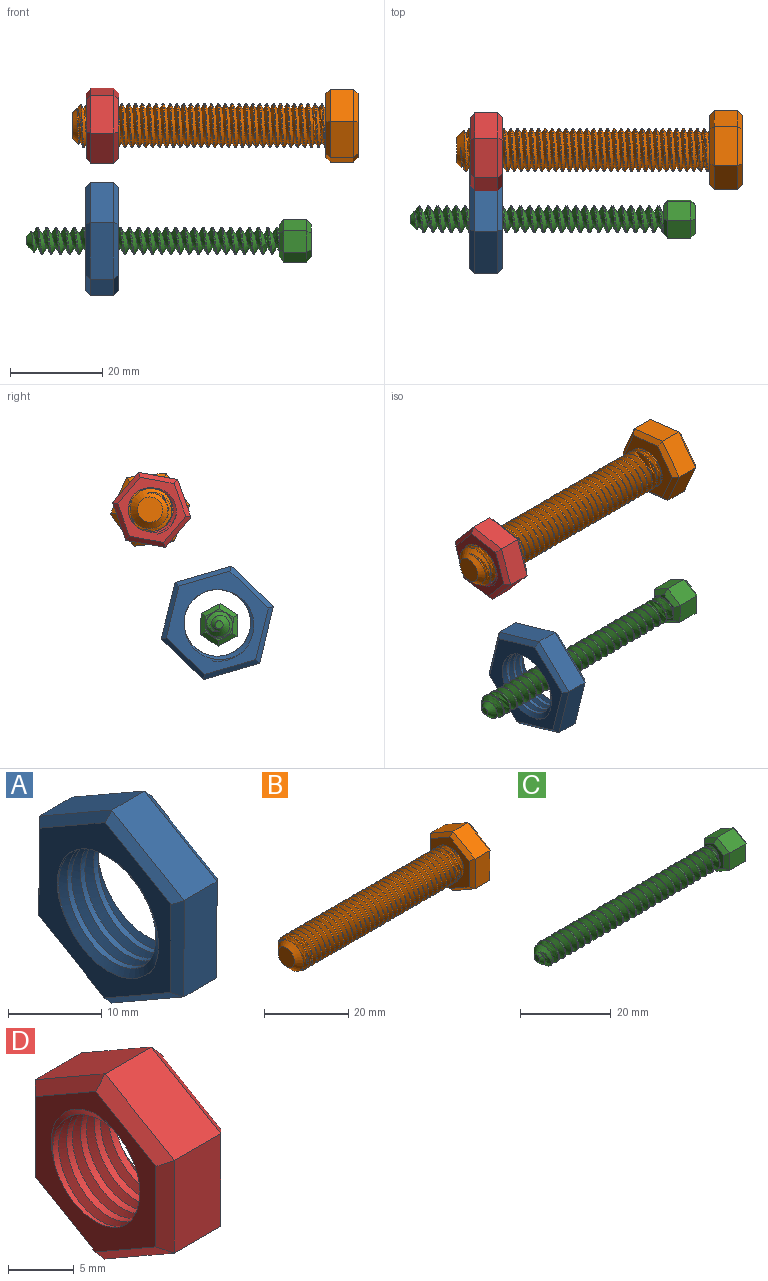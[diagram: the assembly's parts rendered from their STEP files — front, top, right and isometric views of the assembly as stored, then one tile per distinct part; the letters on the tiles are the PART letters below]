
ASSEMBLY  parts=4 mates=2
PART A: 23 faces, bbox 9.3x22.7x26 mm
  f0: cylinder r=7.24mm len=14.48mm, axis (1,0,0), area 111.6mm2, adj f7,f8,f21,f22
  f1: plane 10.98x6.38mm, normal (0,-0.5,0.86), area 63.5mm2, adj f2,f6,f14,f18
  f2: plane 12.7x5mm, normal (0,-1,0), area 63.5mm2, adj f1,f3,f12,f16
  f3: plane 11.02x6.32mm, normal (0,-0.5,-0.87), area 63.5mm2, adj f2,f4,f10,f15
  f4: plane 10.98x6.38mm, normal (0,0.5,-0.86), area 63.5mm2, adj f3,f5,f9,f17
  f5: plane 12.7x5mm, normal (0,1,0), area 63.5mm2, adj f4,f6,f11,f19
  f6: plane 11.02x6.32mm, normal (0,0.5,0.87), area 63.5mm2, adj f1,f5,f13,f20
  f7: plane 23.73x20.67mm, normal (-1,0,0), area 164.4mm2, adj f0,f9,f10,f11,f12,f13,f14,f21
  f8: plane 23.73x20.67mm, normal (1,0,0), area 164.4mm2, adj f0,f15,f16,f17,f18,f19,f20,f21
  f9: plane 10.99x6.96mm, normal (-0.71,0.36,-0.61), area 17.1mm2, adj f4,f7,f10,f11
  f10: plane 11.02x6.9mm, normal (-0.71,-0.35,-0.61), area 17.1mm2, adj f3,f7,f9,f12
  f11: plane 12.7x1.03mm, normal (-0.71,0.71,0), area 17.1mm2, adj f5,f7,f9,f13
  f12: plane 12.7x1.03mm, normal (-0.71,-0.71,0), area 17.1mm2, adj f2,f7,f10,f14
  f13: plane 11.02x6.9mm, normal (-0.71,0.35,0.61), area 17.1mm2, adj f6,f7,f11,f14
  f14: plane 10.99x6.96mm, normal (-0.71,-0.36,0.61), area 17.1mm2, adj f1,f7,f12,f13
  f15: plane 11.02x6.9mm, normal (0.71,-0.35,-0.61), area 17.1mm2, adj f3,f8,f16,f17
  f16: plane 12.7x1.03mm, normal (0.71,-0.71,0), area 17.1mm2, adj f2,f8,f15,f18
  f17: plane 10.99x6.96mm, normal (0.71,0.36,-0.61), area 17.1mm2, adj f4,f8,f15,f19
  f18: plane 10.99x6.96mm, normal (0.71,-0.36,0.61), area 17.1mm2, adj f1,f8,f16,f20
  f19: plane 12.7x1.03mm, normal (0.71,0.71,0), area 17.1mm2, adj f5,f8,f17,f20
  f20: plane 11.02x6.9mm, normal (0.71,0.35,0.61), area 17.1mm2, adj f6,f8,f18,f19
  f21: bspline ~19.31x16.73mm, area 223mm2, adj f0,f7,f8,f22
  f22: bspline ~19.31x16.73mm, area 223mm2, adj f0,f7,f8,f21
PART B: 25 faces, bbox 62.8x15.9x18.1 mm
  f0: cylinder r=4.75mm len=53mm, axis (1,0,0), area 256.1mm2, adj f1,f2,f4,f12
  f1: bspline ~55.16x10.97mm, area 1234.9mm2, adj f0,f2,f4,f12
  f2: bspline ~55.66x10.97mm, area 1234.1mm2, adj f0,f1,f4,f12
  f3: plane 5.5x5.5mm, normal (-1,0,0), area 23.8mm2, adj f4
  f4: cone r=4.75mm half-angle=45deg, axis (1,0,0), area 47.4mm2, adj f0,f1,f2,f3
  f5: plane 7.48x5mm, normal (0,-0.5,0.86), area 43.3mm2, adj f6,f10,f18,f22
  f6: plane 8.66x5mm, normal (0,-1,0), area 43.3mm2, adj f5,f7,f16,f20
  f7: plane 7.52x5mm, normal (0,-0.5,-0.87), area 43.3mm2, adj f6,f8,f14,f19
  f8: plane 7.48x5mm, normal (0,0.5,-0.86), area 43.3mm2, adj f7,f9,f13,f21
  f9: plane 8.66x5mm, normal (0,1,0), area 43.3mm2, adj f8,f10,f15,f23
  f10: plane 7.52x5mm, normal (0,0.5,0.87), area 43.3mm2, adj f5,f9,f17,f24
  f11: plane 15.01x13.03mm, normal (1,0,0), area 146.4mm2, adj f13,f14,f15,f16,f17,f18
  f12: plane 15.83x13.85mm, normal (-1,0,0), area 89.2mm2, adj f0,f1,f2,f19,f20,f21,f22,f23
  f13: plane 7.49x4.93mm, normal (0.71,0.36,-0.61), area 11.4mm2, adj f8,f11,f14,f15
  f14: plane 7.52x4.88mm, normal (0.71,-0.35,-0.61), area 11.4mm2, adj f7,f11,f13,f16
  f15: plane 8.66x1.03mm, normal (0.71,0.71,0), area 11.4mm2, adj f9,f11,f13,f17
  f16: plane 8.66x1.03mm, normal (0.71,-0.71,0), area 11.4mm2, adj f6,f11,f14,f18
  f17: plane 7.52x4.88mm, normal (0.71,0.35,0.61), area 11.4mm2, adj f10,f11,f15,f18
  f18: plane 7.49x4.93mm, normal (0.71,-0.36,0.61), area 11.4mm2, adj f5,f11,f16,f17
  f19: plane 7.52x4.88mm, normal (-0.71,-0.35,-0.61), area 11.4mm2, adj f7,f12,f20,f21
  f20: plane 8.66x1.03mm, normal (-0.71,-0.71,0), area 11.4mm2, adj f6,f12,f19,f22
  f21: plane 7.49x4.93mm, normal (-0.71,0.36,-0.61), area 11.4mm2, adj f8,f12,f19,f23
  f22: plane 7.49x4.93mm, normal (-0.71,-0.36,0.61), area 11.4mm2, adj f5,f12,f20,f24
  f23: plane 8.66x1.03mm, normal (-0.71,0.71,0), area 11.4mm2, adj f9,f12,f21,f24
  f24: plane 7.52x4.88mm, normal (-0.71,0.35,0.61), area 11.4mm2, adj f10,f12,f22,f23
PART C: 25 faces, bbox 63.7x9x10.2 mm
  f0: cylinder r=2.88mm len=53mm, axis (1,0,0), area 76.1mm2, adj f1,f2,f4,f12
  f1: bspline ~55.88x6.65mm, area 631.1mm2, adj f0,f2,f4,f12
  f2: bspline ~56.88x6.65mm, area 636mm2, adj f0,f1,f4,f12
  f3: plane 1.76x1.76mm, normal (-1,0,0), area 2.4mm2, adj f4
  f4: cone r=2.88mm half-angle=45deg, axis (1,0,0), area 19.4mm2, adj f0,f1,f2,f3
  f5: plane 5x3.98mm, normal (0,-0.51,0.86), area 23.1mm2, adj f6,f10,f18,f22
  f6: plane 5x4.62mm, normal (0,-1,-0.01), area 23.1mm2, adj f5,f7,f16,f20
  f7: plane 5x4.02mm, normal (0,-0.49,-0.87), area 23.1mm2, adj f6,f8,f14,f19
  f8: plane 5x3.98mm, normal (0,0.51,-0.86), area 23.1mm2, adj f7,f9,f13,f21
  f9: plane 5x4.62mm, normal (0,1,0.01), area 23.1mm2, adj f8,f10,f15,f23
  f10: plane 5x4.02mm, normal (0,0.49,0.87), area 23.1mm2, adj f5,f9,f17,f24
  f11: plane 6.93x6.03mm, normal (1,0,0), area 31.2mm2, adj f13,f14,f15,f16,f17,f18
  f12: plane 7.92x7.03mm, normal (-1,0,0), area 15mm2, adj f0,f1,f2,f19,f20,f21,f22,f23
  f13: plane 3.99x2.91mm, normal (0.71,0.36,-0.61), area 5.7mm2, adj f8,f11,f14,f15
  f14: plane 4.02x2.86mm, normal (0.71,-0.35,-0.62), area 5.7mm2, adj f7,f11,f13,f16
  f15: plane 4.62x1.03mm, normal (0.71,0.71,0.01), area 5.7mm2, adj f9,f11,f13,f17
  f16: plane 4.62x1.03mm, normal (0.71,-0.71,-0.01), area 5.7mm2, adj f6,f11,f14,f18
  f17: plane 4.02x2.86mm, normal (0.71,0.35,0.62), area 5.7mm2, adj f10,f11,f15,f18
  f18: plane 3.99x2.91mm, normal (0.71,-0.36,0.61), area 5.7mm2, adj f5,f11,f16,f17
  f19: plane 4.02x2.86mm, normal (-0.71,-0.35,-0.62), area 5.7mm2, adj f7,f12,f20,f21
  f20: plane 4.62x1.03mm, normal (-0.71,-0.71,-0.01), area 5.7mm2, adj f6,f12,f19,f22
  f21: plane 3.99x2.91mm, normal (-0.71,0.36,-0.61), area 5.7mm2, adj f8,f12,f19,f23
  f22: plane 3.99x2.91mm, normal (-0.71,-0.36,0.61), area 5.7mm2, adj f5,f12,f20,f24
  f23: plane 4.62x1.03mm, normal (-0.71,0.71,0.01), area 5.7mm2, adj f9,f12,f21,f24
  f24: plane 4.02x2.86mm, normal (-0.71,0.35,0.62), area 5.7mm2, adj f10,f12,f22,f23
PART D: 23 faces, bbox 9.1x15.4x17.7 mm
  f0: plane 7.49x5mm, normal (0,-0.5,0.86), area 43.3mm2, adj f1,f5,f13,f17
  f1: plane 8.66x5mm, normal (0,-1,0), area 43.3mm2, adj f0,f2,f11,f15
  f2: plane 7.51x5mm, normal (0,-0.5,-0.87), area 43.3mm2, adj f1,f3,f9,f14
  f3: plane 7.49x5mm, normal (0,0.5,-0.86), area 43.3mm2, adj f2,f4,f8,f16
  f4: plane 8.66x5mm, normal (0,1,0), area 43.3mm2, adj f3,f5,f10,f18
  f5: plane 7.51x5mm, normal (0,0.5,0.87), area 43.3mm2, adj f0,f4,f12,f19
  f6: plane 15.37x13.38mm, normal (-1,0,0), area 71.4mm2, adj f8,f9,f10,f11,f12,f13,f20,f21
  f7: plane 15.37x13.38mm, normal (1,0,0), area 71.4mm2, adj f14,f15,f16,f17,f18,f19,f20,f21
  f8: plane 7.49x4.93mm, normal (-0.71,0.36,-0.61), area 11.4mm2, adj f3,f6,f9,f10
  f9: plane 7.51x4.89mm, normal (-0.71,-0.35,-0.61), area 11.4mm2, adj f2,f6,f8,f11
  f10: plane 8.66x1.02mm, normal (-0.71,0.71,0), area 11.4mm2, adj f4,f6,f8,f12
  f11: plane 8.66x1.02mm, normal (-0.71,-0.71,0), area 11.4mm2, adj f1,f6,f9,f13
  f12: plane 7.51x4.89mm, normal (-0.71,0.35,0.61), area 11.4mm2, adj f5,f6,f10,f13
  f13: plane 7.49x4.93mm, normal (-0.71,-0.36,0.61), area 11.4mm2, adj f0,f6,f11,f12
  f14: plane 7.51x4.89mm, normal (0.71,-0.35,-0.61), area 11.4mm2, adj f2,f7,f15,f16
  f15: plane 8.66x1.02mm, normal (0.71,-0.71,0), area 11.4mm2, adj f1,f7,f14,f17
  f16: plane 7.49x4.93mm, normal (0.71,0.36,-0.61), area 11.4mm2, adj f3,f7,f14,f18
  f17: plane 7.49x4.93mm, normal (0.71,-0.36,0.61), area 11.4mm2, adj f0,f7,f15,f19
  f18: plane 8.66x1.02mm, normal (0.71,0.71,0), area 11.4mm2, adj f4,f7,f16,f19
  f19: plane 7.51x4.89mm, normal (0.71,0.35,0.61), area 11.4mm2, adj f5,f7,f17,f18
  f20: cylinder r=4.66mm len=9.32mm, axis (1,0,0), area 85.4mm2, adj f6,f7,f21,f22
  f21: bspline ~12.5x10.82mm, area 128.4mm2, adj f6,f7,f20,f22
  f22: bspline ~12.5x10.82mm, area 128.5mm2, adj f6,f7,f20,f21
PLACE A rot(axis=(0,0.6,-0.8),180deg) t=(-55.27,-6.86,23.48)mm fixed
PLACE B rot(axis=(1,0,0),143.4deg) t=(0.34,7.73,48.08)mm
PLACE C rot(axis=(-1,0,0),178.1deg) t=(-9.77,-7.25,23.06)mm
PLACE D rot(axis=(1,0,0),100.2deg) t=(-48.16,7.38,48.02)mm fixed
MATE cylindrical C.f0 <-> A.f7  axis (-1,0,0) through (-68.27,-7.25,23.06)mm
MATE cylindrical B.f0 <-> D.f6  axis (-1,0,0) through (-58.16,7.73,48.08)mm
